# Revit family: Thorn EQUALINE CL
name_source: partatom
category: Lighting Fixtures
revit_build: Autodesk Revit 2016 (Build: 20150220_1215(x64)
units: mm (PartAtom-declared; Revit-internal decimal feet)

## family parameters
Cut with Voids When Loaded = No
Host = Face
Light Source = Yes
OmniClass Number = 23.80.70.11
OmniClass Title = Luminaries for Internal Lighting
Part Type = Normal
Room Calculation Point = No
Round Connector Dimension = Use Diameter
Shared = No

## types (3) — shared parameters
Apparent Load = 11 VA
Assembly Code = D5020200
Color Filter = 16777215
Color Light Emitting Surface = Thorn_PMMA_White
Description = LED light line corner
Dimming Lamp Color Temperature Shift = <None>
Emit Shape Visible in Rendering = No
Emit from Rectangle Length = 72 mm  [stored 0.23622 ft]
Emit from Rectangle Width = 541 mm  [stored 1.77493 ft]
Height = 88 mm  [stored 0.288714 ft]
Lamp = LED
Length = 541 mm  [stored 1.77493 ft]
Manufacturer = Thorn Lighting
Tilt Angle = -90.00°
URL = http://www.thornlighting.com
Voltage = 230 V
Width = 541 mm  [stored 1.77493 ft]
zero-valued in all types: Default Elevation

## per-type parameters (varying)
| type | Body | F Frame | FS Frame | Model | Photometric Web File |
| EQL CL L541 | Thorn_Metal_Silver | No | No | 96631961 | D41200AA_EQL_CL_C_L500_840_PM_SR.IES |
| EQL CL C L553 F | Thorn_Metal_White | Yes | No | 96631962 | D41197AA_EQL_CL_C_L500_840_PM_WH.IES |
| EQL CL L546 FS | Thorn_Metal_Silver | No | Yes | 96631958 | D41200AA_EQL_CL_C_L500_840_PM_SR.IES |

note: [stored X ft] marks values corroborated as IEEE doubles in the binary element streams (Revit-internal decimal feet)

## geometry (parser evidence)
native form markers: Sweep x9
no freeform markers — native parametric forms only
